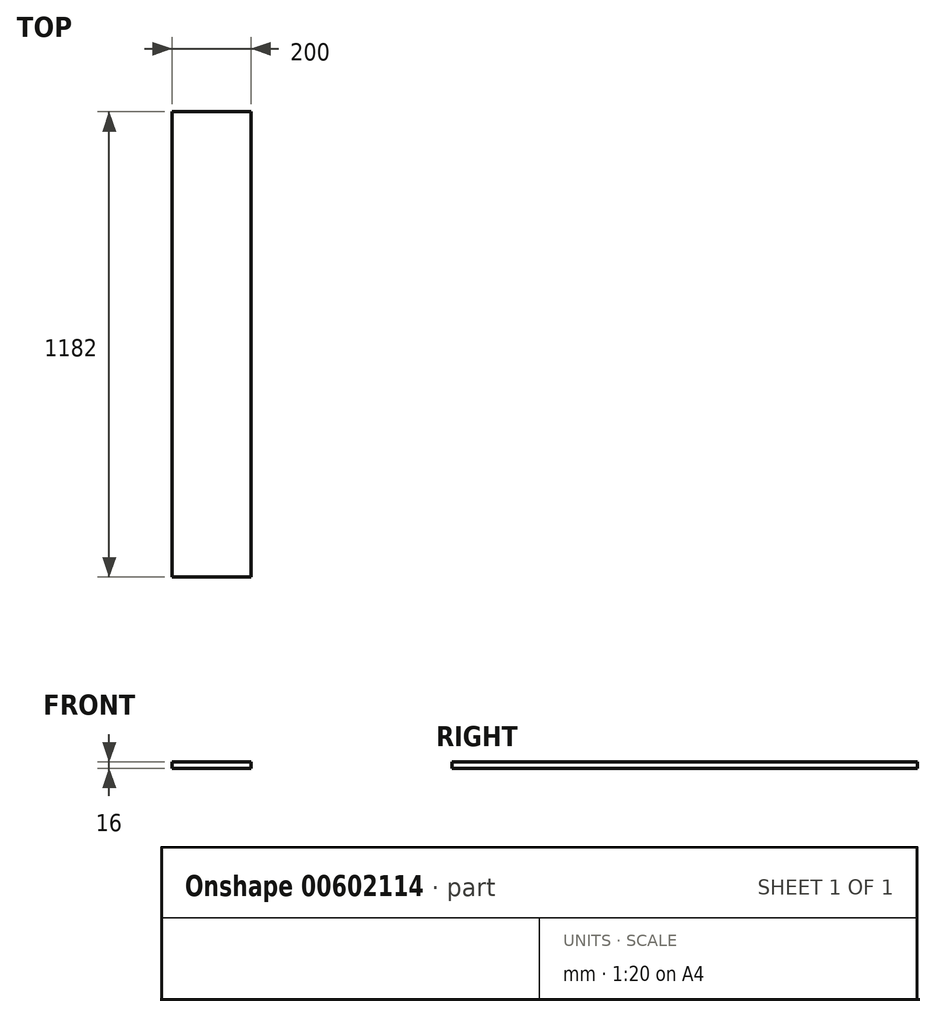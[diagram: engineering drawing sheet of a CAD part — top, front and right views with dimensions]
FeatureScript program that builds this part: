
annotation { "Feature Type Name" : "Feature", "Feature Type Description" : "" }
export const myFeature = defineFeature(function(context is Context, id is Id, definition is map)
    precondition{}
    {
        {
            var Q0;
            Q0=qCreatedBy(makeId("Top.planeOp"),FACE);
            var sketch = newSketch(context, id + "F0", { "sketchPlane" : qUnion([Q0])});
            skLineSegment(sketch, "E0.bottom", {"start": v(0, 0) * mm, "end": v(200, 0) * mm});
            skLineSegment(sketch, "E0.top", {"start": v(0, -1182) * mm, "end": v(200, -1182) * mm});
            skLineSegment(sketch, "E0.left", {"start": v(0, 0) * mm, "end": v(0, -1182) * mm});
            skLineSegment(sketch, "E0.right", {"start": v(200, 0) * mm, "end": v(200, -1182) * mm});
            skSolve(sketch);
        }
        {
            var Q0;
            Q0 = qSketchRegion(id + "F0", true);
            extrude(context, id + "F1", {"entities" : qUnion([Q0]), "depth" : 16 * mm, "offsetDistance" : 25 * mm});
        }
    });
